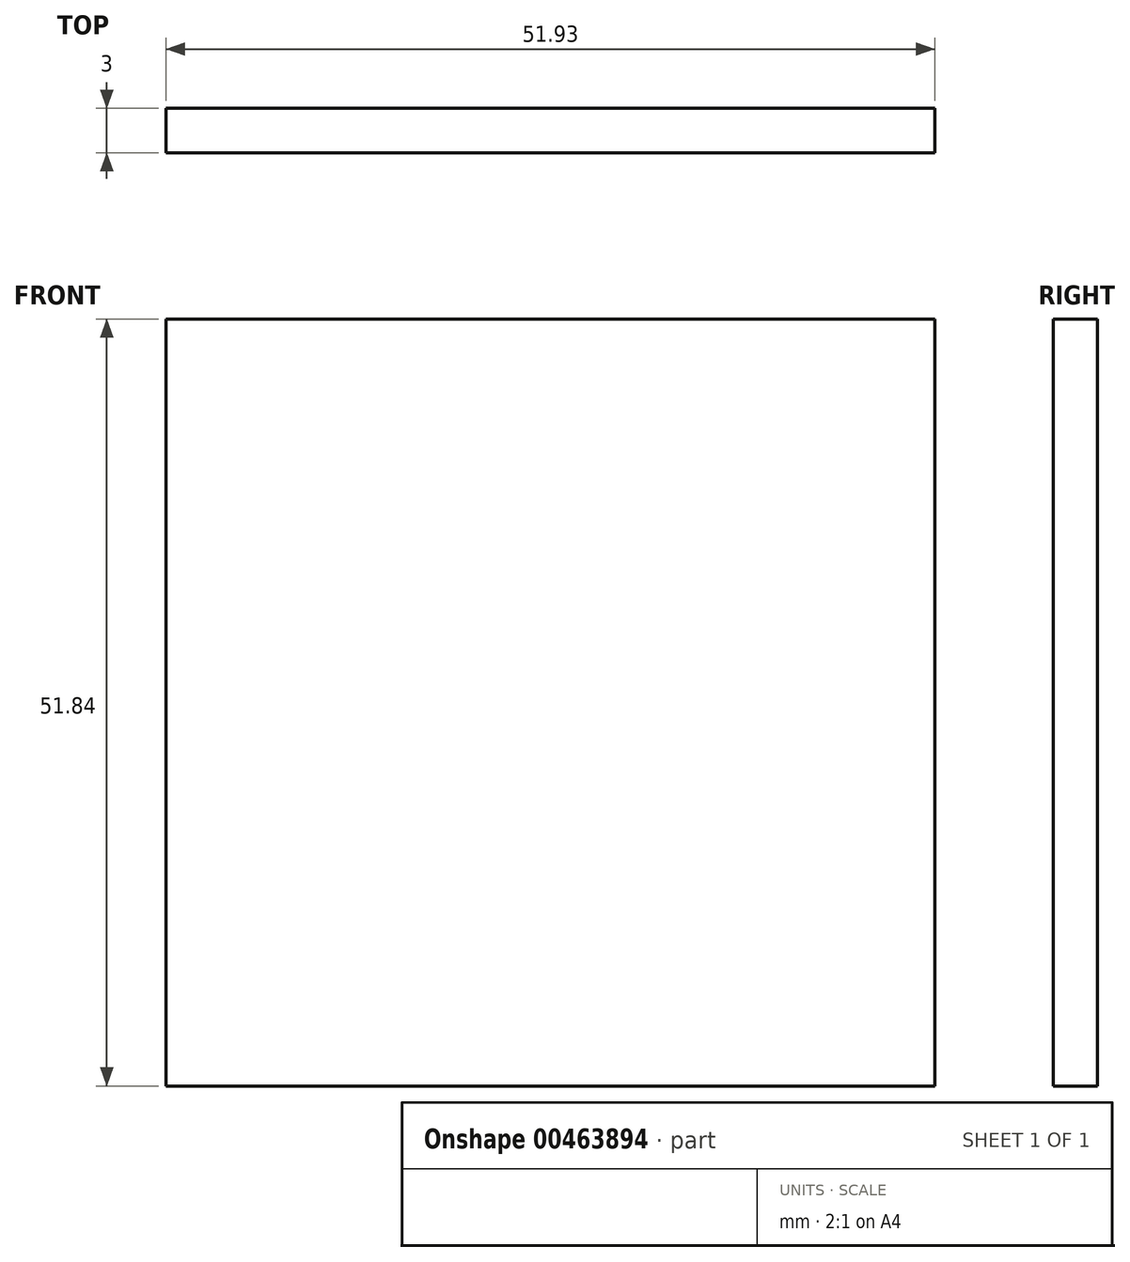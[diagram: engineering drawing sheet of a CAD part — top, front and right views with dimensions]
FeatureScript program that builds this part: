
annotation { "Feature Type Name" : "Feature", "Feature Type Description" : "" }
export const myFeature = defineFeature(function(context is Context, id is Id, definition is map)
    precondition{}
    {
        {
            var Q0;
            Q0=qCreatedBy(makeId("Front.planeOp"),FACE);
            var sketch = newSketch(context, id + "F0", { "sketchPlane" : qUnion([Q0])});
            skLineSegment(sketch, "E0.bottom", {"start": v(-67.21, 51.84) * mm, "end": v(-15.28, 51.84) * mm});
            skLineSegment(sketch, "E0.top", {"start": v(-67.21, 0) * mm, "end": v(-15.28, 0) * mm});
            skLineSegment(sketch, "E0.left", {"start": v(-67.21, 51.84) * mm, "end": v(-67.21, 0) * mm});
            skLineSegment(sketch, "E0.right", {"start": v(-15.28, 51.84) * mm, "end": v(-15.28, 0) * mm});
            skSolve(sketch);
        }
        {
            var Q0;
            Q0=makeQuery(id+"F0.imprint","IMPRINT",FACE,{"disambiguationData":[TD([[makeQuery(id+"F0.imprint","IMPRINT",EDGE,{"derivedFrom":sQuery(id+"F0.wireOp",EDGE,"E0.bottom")}),-1.0]])]});
            extrude(context, id + "F1", {"entities" : qUnion([Q0]), "depth" : 3 * mm});
        }
    });
